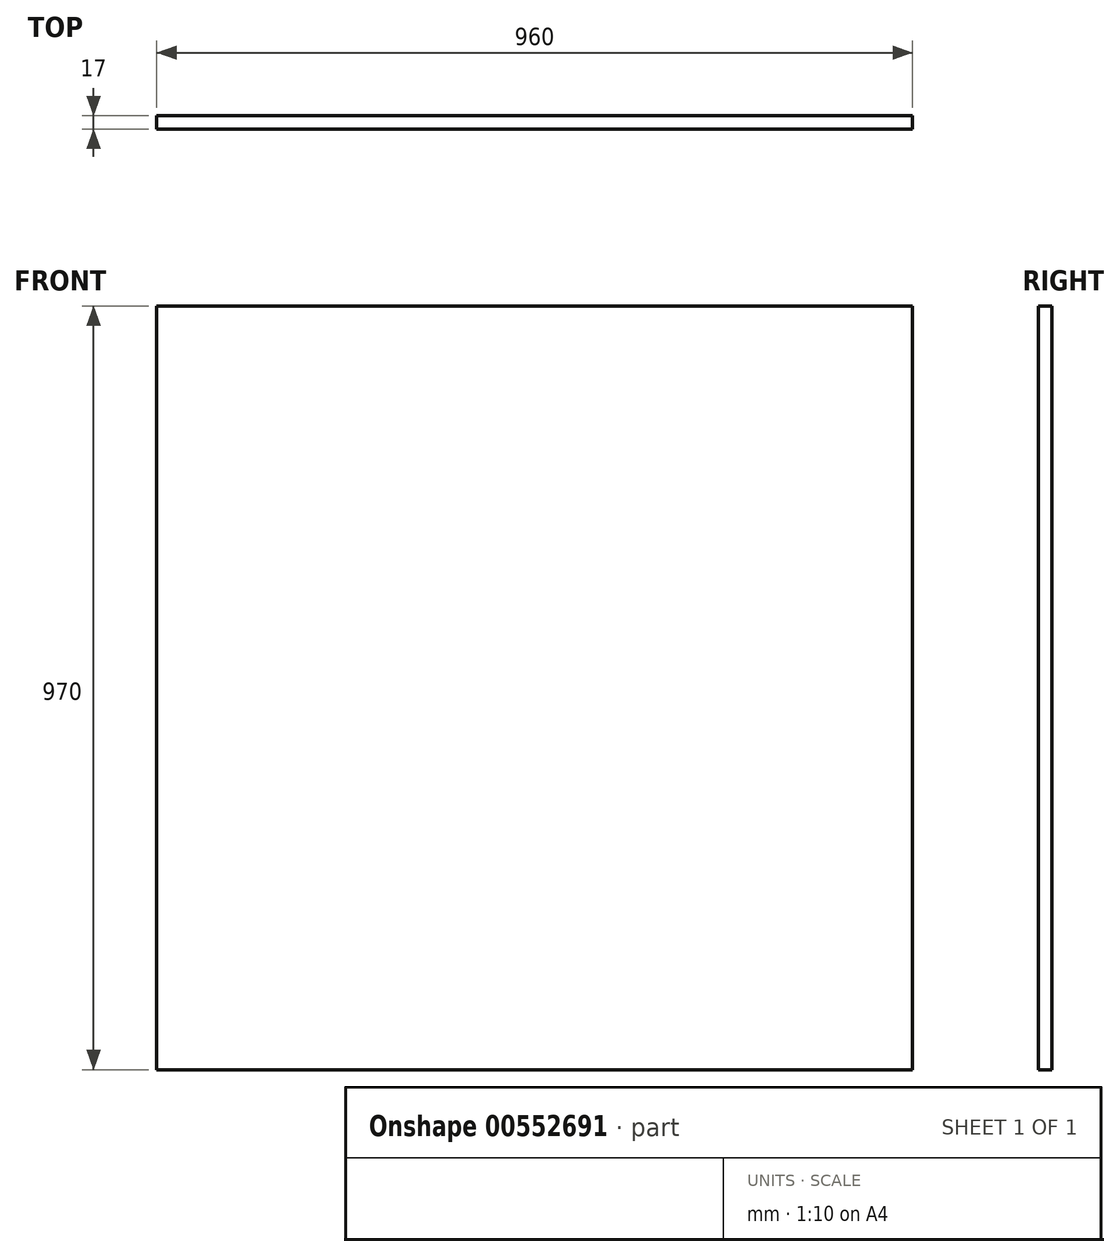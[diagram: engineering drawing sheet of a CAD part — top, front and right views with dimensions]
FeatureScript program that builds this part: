
annotation { "Feature Type Name" : "Feature", "Feature Type Description" : "" }
export const myFeature = defineFeature(function(context is Context, id is Id, definition is map)
    precondition{}
    {
        {
            var Q0;
            Q0=qCreatedBy(makeId("Front.planeOp"),FACE);
            var sketch = newSketch(context, id + "F0", { "sketchPlane" : qUnion([Q0])});
            skLineSegment(sketch, "E0.bottom", {"start": v(480, 485) * mm, "end": v(-480, 485) * mm});
            skLineSegment(sketch, "E0.top", {"start": v(480, -485) * mm, "end": v(-480, -485) * mm});
            skLineSegment(sketch, "E0.left", {"start": v(480, 485) * mm, "end": v(480, -485) * mm});
            skLineSegment(sketch, "E0.right", {"start": v(-480, 485) * mm, "end": v(-480, -485) * mm});
            skPoint(sketch, "E0.middle", {"position": v(0, 0) * mm});
            skSolve(sketch);
        }
        {
            var Q0;
            Q0 = qSketchRegion(id + "F0", true);
            extrude(context, id + "F1", {"entities" : qUnion([Q0]), "oppositeDirection" : true, "depth" : 17 * mm, "offsetDistance" : 25 * mm});
        }
    });
